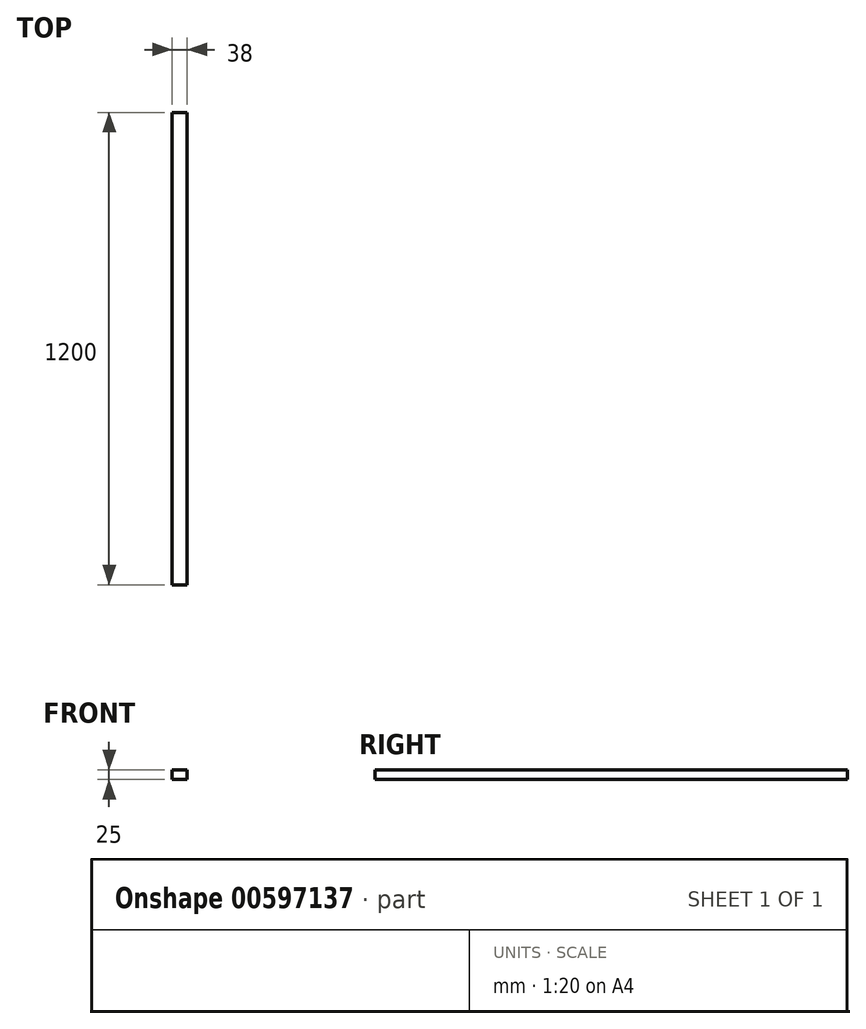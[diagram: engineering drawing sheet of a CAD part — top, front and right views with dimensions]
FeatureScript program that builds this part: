
annotation { "Feature Type Name" : "Feature", "Feature Type Description" : "" }
export const myFeature = defineFeature(function(context is Context, id is Id, definition is map)
    precondition{}
    {
        {
            var Q0;
            Q0=qCreatedBy(makeId("Front.planeOp"),FACE);
            var sketch = newSketch(context, id + "F0", { "sketchPlane" : qUnion([Q0])});
            skLineSegment(sketch, "E0.bottom", {"start": v(19, 12.5) * mm, "end": v(-19, 12.5) * mm});
            skLineSegment(sketch, "E0.top", {"start": v(19, -12.5) * mm, "end": v(-19, -12.5) * mm});
            skLineSegment(sketch, "E0.left", {"start": v(19, 12.5) * mm, "end": v(19, -12.5) * mm});
            skLineSegment(sketch, "E0.right", {"start": v(-19, 12.5) * mm, "end": v(-19, -12.5) * mm});
            skPoint(sketch, "E0.middle", {"position": v(0, 0) * mm});
            skSolve(sketch);
        }
        {
            var Q0;
            Q0 = qSketchRegion(id + "F0", true);
            extrude(context, id + "F1", {"entities" : qUnion([Q0]), "depth" : 1200 * mm, "offsetDistance" : 25 * mm});
        }
    });
